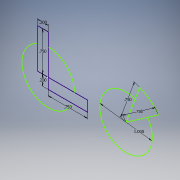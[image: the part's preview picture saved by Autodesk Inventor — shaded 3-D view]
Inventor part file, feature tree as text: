
AUTODESK INVENTOR PART (.ipt)
format: ipt  version: 2019 (Build 230136000, 136)  size: 97,280 bytes
history: native  units: in
note: dims shown in document units (in); Inventor stores cm internally (conversion verified against a paired STEP export)
features: sketch x1
ambient origin geometry x8: Origin, YZ Plane, XZ Plane, XY Plane, X Axis, Y Axis, Z Axis, Center Point
feature tree (1):
  sketch  "Sketch1"  dims[d0=1.0in d7=1.0in d8=0.75in d9=0.2in d10=0.2in d11=0.75in d12=0.75in d13=0.75in]
